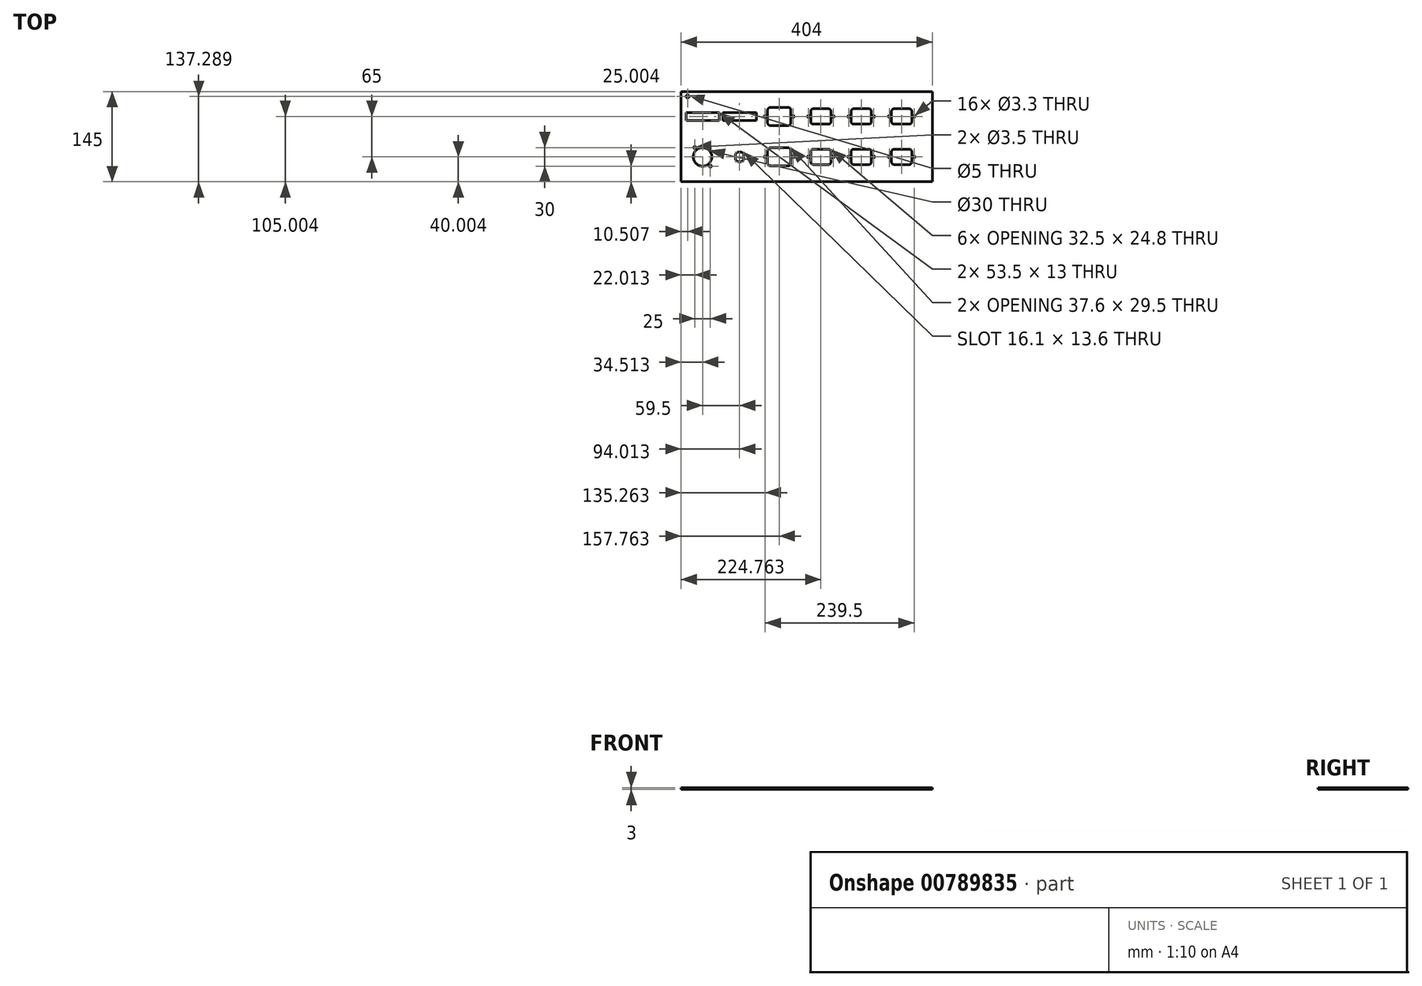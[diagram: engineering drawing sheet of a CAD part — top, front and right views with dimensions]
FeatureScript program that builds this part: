
annotation { "Feature Type Name" : "Feature", "Feature Type Description" : "" }
export const myFeature = defineFeature(function(context is Context, id is Id, definition is map)
    precondition{}
    {
        {
            var Q0;
            Q0=qCreatedBy(makeId("Top.planeOp"),FACE);
            var sketch = newSketch(context, id + "F0", { "sketchPlane" : qUnion([Q0])});
            skLineSegment(sketch, "E0.bottom", {"start": v(-216.19, 64.87) * mm, "end": v(187.81, 64.87) * mm});
            skLineSegment(sketch, "E0.top", {"start": v(-216.19, -80.13) * mm, "end": v(187.81, -80.13) * mm});
            skLineSegment(sketch, "E0.left", {"start": v(-216.19, 64.87) * mm, "end": v(-216.19, -80.13) * mm});
            skLineSegment(sketch, "E0.right", {"start": v(187.81, 64.87) * mm, "end": v(187.81, -80.13) * mm});
            skSolve(sketch);
        }
        {
            var Q0;
            Q0=qCreatedBy(makeId("Top.planeOp"),FACE);
            var sketch = newSketch(context, id + "F1", { "sketchPlane" : qUnion([Q0])});
            skLineSegment(sketch, "E1.bottom", {"start": v(150.82, 12.47) * mm, "end": v(126.32, 12.47) * mm});
            skLineSegment(sketch, "E1.top", {"start": v(150.82, 37.27) * mm, "end": v(126.32, 37.27) * mm});
            skLineSegment(sketch, "E1.left", {"start": v(154.82, 16.47) * mm, "end": v(154.82, 33.27) * mm});
            skLineSegment(sketch, "E1.right", {"start": v(122.32, 16.47) * mm, "end": v(122.32, 33.27) * mm});
            skPoint(sketch, "E1.middle", {"position": v(138.57, 24.87) * mm});
            skPoint(sketch, "E2.visualSharp", {"position": v(122.32, 37.27) * mm});
            skArc(sketch, "E2.filletArc", {"start": v(126.32, 37.27) * mm, "mid": v(123.5, 36.1) * mm, "end": v(122.32, 33.27) * mm});
            skPoint(sketch, "E3.visualSharp", {"position": v(154.82, 37.27) * mm});
            skArc(sketch, "E3.filletArc", {"start": v(154.82, 33.27) * mm, "mid": v(153.65, 36.1) * mm, "end": v(150.82, 37.27) * mm});
            skPoint(sketch, "E4.visualSharp", {"position": v(154.82, 12.47) * mm});
            skArc(sketch, "E4.filletArc", {"start": v(150.82, 12.47) * mm, "mid": v(153.65, 13.65) * mm, "end": v(154.82, 16.47) * mm});
            skPoint(sketch, "E5.visualSharp", {"position": v(122.32, 12.47) * mm});
            skArc(sketch, "E5.filletArc", {"start": v(122.32, 16.47) * mm, "mid": v(123.5, 13.65) * mm, "end": v(126.32, 12.47) * mm});
            skCircle(sketch, "E6", {"center": v(158.57, 24.87) * mm, "radius": 1.5 * mm});
            skCircle(sketch, "E7", {"center": v(118.57, 24.87) * mm, "radius": 1.5 * mm});
            skLineSegment(sketch, "E8.bottom", {"start": v(-44.63, 10.12) * mm, "end": v(-72.23, 10.12) * mm});
            skLineSegment(sketch, "E8.top", {"start": v(-44.63, 39.62) * mm, "end": v(-72.23, 39.62) * mm});
            skLineSegment(sketch, "E8.left", {"start": v(-39.63, 15.12) * mm, "end": v(-39.63, 34.62) * mm});
            skLineSegment(sketch, "E8.right", {"start": v(-77.23, 15.12) * mm, "end": v(-77.23, 34.62) * mm});
            skPoint(sketch, "E8.middle", {"position": v(-58.43, 24.87) * mm});
            skPoint(sketch, "E9.visualSharp", {"position": v(-77.23, 39.62) * mm});
            skArc(sketch, "E9.filletArc", {"start": v(-72.23, 39.62) * mm, "mid": v(-75.76, 38.16) * mm, "end": v(-77.23, 34.62) * mm});
            skPoint(sketch, "E10.visualSharp", {"position": v(-39.63, 39.62) * mm});
            skArc(sketch, "E10.filletArc", {"start": v(-39.63, 34.62) * mm, "mid": v(-41.1, 38.16) * mm, "end": v(-44.63, 39.62) * mm});
            skPoint(sketch, "E11.visualSharp", {"position": v(-39.63, 10.12) * mm});
            skArc(sketch, "E11.filletArc", {"start": v(-44.63, 10.12) * mm, "mid": v(-41.1, 11.59) * mm, "end": v(-39.63, 15.12) * mm});
            skPoint(sketch, "E12.visualSharp", {"position": v(-77.23, 10.12) * mm});
            skArc(sketch, "E12.filletArc", {"start": v(-77.23, 15.12) * mm, "mid": v(-75.76, 11.59) * mm, "end": v(-72.23, 10.12) * mm});
            skCircle(sketch, "E13", {"center": v(-35.93, 24.87) * mm, "radius": 1.5 * mm});
            skCircle(sketch, "E14", {"center": v(-80.93, 24.87) * mm, "radius": 1.5 * mm});
            skLineSegment(sketch, "E15", {"start": v(-85.43, 7.87) * mm, "end": v(-85.43, 41.87) * mm, "construction": true});
            skLineSegment(sketch, "E16", {"start": v(-85.43, 41.87) * mm, "end": v(-31.43, 41.87) * mm, "construction": true});
            skLineSegment(sketch, "E17", {"start": v(-31.43, 41.87) * mm, "end": v(-31.43, 7.87) * mm, "construction": true});
            skLineSegment(sketch, "E18", {"start": v(-31.43, 7.87) * mm, "end": v(-85.43, 7.87) * mm, "construction": true});
            skLineSegment(sketch, "E19", {"start": v(113.57, 38.87) * mm, "end": v(113.57, 10.87) * mm, "construction": true});
            skLineSegment(sketch, "E20", {"start": v(113.57, 10.87) * mm, "end": v(163.57, 10.87) * mm, "construction": true});
            skLineSegment(sketch, "E21", {"start": v(163.57, 10.87) * mm, "end": v(163.57, 38.87) * mm, "construction": true});
            skLineSegment(sketch, "E22", {"start": v(163.57, 38.87) * mm, "end": v(113.57, 38.87) * mm, "construction": true});
            skLineSegment(sketch, "E23.0.1.0", {"start": v(163.57, -26.13) * mm, "end": v(113.57, -26.13) * mm, "construction": true});
            skLineSegment(sketch, "E23.0.1.1", {"start": v(113.57, -26.13) * mm, "end": v(113.57, -54.13) * mm, "construction": true});
            skLineSegment(sketch, "E23.0.1.2", {"start": v(163.57, -54.13) * mm, "end": v(163.57, -26.13) * mm, "construction": true});
            skLineSegment(sketch, "E23.0.1.3", {"start": v(122.32, -48.53) * mm, "end": v(122.32, -31.73) * mm});
            skLineSegment(sketch, "E23.0.1.4", {"start": v(154.82, -48.53) * mm, "end": v(154.82, -31.73) * mm});
            skLineSegment(sketch, "E23.0.1.5", {"start": v(150.82, -27.73) * mm, "end": v(126.32, -27.73) * mm});
            skPoint(sketch, "E23.0.1.6", {"position": v(154.82, -27.73) * mm});
            skLineSegment(sketch, "E23.0.1.7", {"start": v(150.82, -52.53) * mm, "end": v(126.32, -52.53) * mm});
            skLineSegment(sketch, "E23.0.1.8", {"start": v(113.57, -54.13) * mm, "end": v(163.57, -54.13) * mm, "construction": true});
            skPoint(sketch, "E23.0.1.9", {"position": v(138.57, -40.13) * mm});
            skPoint(sketch, "E23.0.1.10", {"position": v(122.32, -52.53) * mm});
            skPoint(sketch, "E23.0.1.11", {"position": v(154.82, -52.53) * mm});
            skPoint(sketch, "E23.0.1.12", {"position": v(122.32, -27.73) * mm});
            skCircle(sketch, "E23.0.1.13", {"center": v(158.57, -40.13) * mm, "radius": 1.5 * mm});
            skCircle(sketch, "E23.0.1.14", {"center": v(118.57, -40.13) * mm, "radius": 1.5 * mm});
            skArc(sketch, "E23.0.1.15", {"start": v(122.32, -48.53) * mm, "mid": v(123.5, -51.35) * mm, "end": v(126.32, -52.53) * mm});
            skArc(sketch, "E23.0.1.16", {"start": v(154.82, -31.73) * mm, "mid": v(153.65, -28.9) * mm, "end": v(150.82, -27.73) * mm});
            skArc(sketch, "E23.0.1.17", {"start": v(150.82, -52.53) * mm, "mid": v(153.65, -51.35) * mm, "end": v(154.82, -48.53) * mm});
            skArc(sketch, "E23.0.1.18", {"start": v(126.32, -27.73) * mm, "mid": v(123.5, -28.9) * mm, "end": v(122.32, -31.73) * mm});
            skLineSegment(sketch, "E23.1.0.0", {"start": v(98.57, 38.87) * mm, "end": v(48.57, 38.87) * mm, "construction": true});
            skLineSegment(sketch, "E23.1.0.1", {"start": v(48.57, 38.87) * mm, "end": v(48.57, 10.87) * mm, "construction": true});
            skLineSegment(sketch, "E23.1.0.2", {"start": v(98.57, 10.87) * mm, "end": v(98.57, 38.87) * mm, "construction": true});
            skLineSegment(sketch, "E23.1.0.3", {"start": v(57.32, 16.47) * mm, "end": v(57.32, 33.27) * mm});
            skLineSegment(sketch, "E23.1.0.4", {"start": v(89.82, 16.47) * mm, "end": v(89.82, 33.27) * mm});
            skLineSegment(sketch, "E23.1.0.5", {"start": v(85.82, 37.27) * mm, "end": v(61.32, 37.27) * mm});
            skPoint(sketch, "E23.1.0.6", {"position": v(89.82, 37.27) * mm});
            skLineSegment(sketch, "E23.1.0.7", {"start": v(85.82, 12.47) * mm, "end": v(61.32, 12.47) * mm});
            skLineSegment(sketch, "E23.1.0.8", {"start": v(48.57, 10.87) * mm, "end": v(98.57, 10.87) * mm, "construction": true});
            skPoint(sketch, "E23.1.0.9", {"position": v(73.57, 24.87) * mm});
            skPoint(sketch, "E23.1.0.10", {"position": v(57.32, 12.47) * mm});
            skPoint(sketch, "E23.1.0.11", {"position": v(89.82, 12.47) * mm});
            skPoint(sketch, "E23.1.0.12", {"position": v(57.32, 37.27) * mm});
            skCircle(sketch, "E23.1.0.13", {"center": v(93.57, 24.87) * mm, "radius": 1.5 * mm});
            skCircle(sketch, "E23.1.0.14", {"center": v(53.57, 24.87) * mm, "radius": 1.5 * mm});
            skArc(sketch, "E23.1.0.15", {"start": v(57.32, 16.47) * mm, "mid": v(58.5, 13.65) * mm, "end": v(61.32, 12.47) * mm});
            skArc(sketch, "E23.1.0.16", {"start": v(89.82, 33.27) * mm, "mid": v(88.65, 36.1) * mm, "end": v(85.82, 37.27) * mm});
            skArc(sketch, "E23.1.0.17", {"start": v(85.82, 12.47) * mm, "mid": v(88.65, 13.65) * mm, "end": v(89.82, 16.47) * mm});
            skArc(sketch, "E23.1.0.18", {"start": v(61.32, 37.27) * mm, "mid": v(58.5, 36.1) * mm, "end": v(57.32, 33.27) * mm});
            skLineSegment(sketch, "E23.1.1.0", {"start": v(98.57, -26.13) * mm, "end": v(48.57, -26.13) * mm, "construction": true});
            skLineSegment(sketch, "E23.1.1.1", {"start": v(48.57, -26.13) * mm, "end": v(48.57, -54.13) * mm, "construction": true});
            skLineSegment(sketch, "E23.1.1.2", {"start": v(98.57, -54.13) * mm, "end": v(98.57, -26.13) * mm, "construction": true});
            skLineSegment(sketch, "E23.1.1.3", {"start": v(57.32, -48.53) * mm, "end": v(57.32, -31.73) * mm});
            skLineSegment(sketch, "E23.1.1.4", {"start": v(89.82, -48.53) * mm, "end": v(89.82, -31.73) * mm});
            skLineSegment(sketch, "E23.1.1.5", {"start": v(85.82, -27.73) * mm, "end": v(61.32, -27.73) * mm});
            skPoint(sketch, "E23.1.1.6", {"position": v(89.82, -27.73) * mm});
            skLineSegment(sketch, "E23.1.1.7", {"start": v(85.82, -52.53) * mm, "end": v(61.32, -52.53) * mm});
            skLineSegment(sketch, "E23.1.1.8", {"start": v(48.57, -54.13) * mm, "end": v(98.57, -54.13) * mm, "construction": true});
            skPoint(sketch, "E23.1.1.9", {"position": v(73.57, -40.13) * mm});
            skPoint(sketch, "E23.1.1.10", {"position": v(57.32, -52.53) * mm});
            skPoint(sketch, "E23.1.1.11", {"position": v(89.82, -52.53) * mm});
            skPoint(sketch, "E23.1.1.12", {"position": v(57.32, -27.73) * mm});
            skCircle(sketch, "E23.1.1.13", {"center": v(93.57, -40.13) * mm, "radius": 1.5 * mm});
            skCircle(sketch, "E23.1.1.14", {"center": v(53.57, -40.13) * mm, "radius": 1.5 * mm});
            skArc(sketch, "E23.1.1.15", {"start": v(57.32, -48.53) * mm, "mid": v(58.5, -51.35) * mm, "end": v(61.32, -52.53) * mm});
            skArc(sketch, "E23.1.1.16", {"start": v(89.82, -31.73) * mm, "mid": v(88.65, -28.9) * mm, "end": v(85.82, -27.73) * mm});
            skArc(sketch, "E23.1.1.17", {"start": v(85.82, -52.53) * mm, "mid": v(88.65, -51.35) * mm, "end": v(89.82, -48.53) * mm});
            skArc(sketch, "E23.1.1.18", {"start": v(61.32, -27.73) * mm, "mid": v(58.5, -28.9) * mm, "end": v(57.32, -31.73) * mm});
            skLineSegment(sketch, "E23.2.0.0", {"start": v(33.57, 38.87) * mm, "end": v(-16.43, 38.87) * mm, "construction": true});
            skLineSegment(sketch, "E23.2.0.1", {"start": v(-16.43, 38.87) * mm, "end": v(-16.43, 10.87) * mm, "construction": true});
            skLineSegment(sketch, "E23.2.0.2", {"start": v(33.57, 10.87) * mm, "end": v(33.57, 38.87) * mm, "construction": true});
            skLineSegment(sketch, "E23.2.0.3", {"start": v(-7.68, 16.47) * mm, "end": v(-7.68, 33.27) * mm});
            skLineSegment(sketch, "E23.2.0.4", {"start": v(24.82, 16.47) * mm, "end": v(24.82, 33.27) * mm});
            skLineSegment(sketch, "E23.2.0.5", {"start": v(20.82, 37.27) * mm, "end": v(-3.68, 37.27) * mm});
            skPoint(sketch, "E23.2.0.6", {"position": v(24.82, 37.27) * mm});
            skLineSegment(sketch, "E23.2.0.7", {"start": v(20.82, 12.47) * mm, "end": v(-3.68, 12.47) * mm});
            skLineSegment(sketch, "E23.2.0.8", {"start": v(-16.43, 10.87) * mm, "end": v(33.57, 10.87) * mm, "construction": true});
            skPoint(sketch, "E23.2.0.9", {"position": v(8.57, 24.87) * mm});
            skPoint(sketch, "E23.2.0.10", {"position": v(-7.68, 12.47) * mm});
            skPoint(sketch, "E23.2.0.11", {"position": v(24.82, 12.47) * mm});
            skPoint(sketch, "E23.2.0.12", {"position": v(-7.68, 37.27) * mm});
            skCircle(sketch, "E23.2.0.13", {"center": v(28.57, 24.87) * mm, "radius": 1.5 * mm});
            skCircle(sketch, "E23.2.0.14", {"center": v(-11.43, 24.87) * mm, "radius": 1.5 * mm});
            skArc(sketch, "E23.2.0.15", {"start": v(-7.68, 16.47) * mm, "mid": v(-6.5, 13.65) * mm, "end": v(-3.68, 12.47) * mm});
            skArc(sketch, "E23.2.0.16", {"start": v(24.82, 33.27) * mm, "mid": v(23.65, 36.1) * mm, "end": v(20.82, 37.27) * mm});
            skArc(sketch, "E23.2.0.17", {"start": v(20.82, 12.47) * mm, "mid": v(23.65, 13.65) * mm, "end": v(24.82, 16.47) * mm});
            skArc(sketch, "E23.2.0.18", {"start": v(-3.68, 37.27) * mm, "mid": v(-6.5, 36.1) * mm, "end": v(-7.68, 33.27) * mm});
            skLineSegment(sketch, "E23.2.1.0", {"start": v(33.57, -26.13) * mm, "end": v(-16.43, -26.13) * mm, "construction": true});
            skLineSegment(sketch, "E23.2.1.1", {"start": v(-16.43, -26.13) * mm, "end": v(-16.43, -54.13) * mm, "construction": true});
            skLineSegment(sketch, "E23.2.1.2", {"start": v(33.57, -54.13) * mm, "end": v(33.57, -26.13) * mm, "construction": true});
            skLineSegment(sketch, "E23.2.1.3", {"start": v(-7.68, -48.53) * mm, "end": v(-7.68, -31.73) * mm});
            skLineSegment(sketch, "E23.2.1.4", {"start": v(24.82, -48.53) * mm, "end": v(24.82, -31.73) * mm});
            skLineSegment(sketch, "E23.2.1.5", {"start": v(20.82, -27.73) * mm, "end": v(-3.68, -27.73) * mm});
            skPoint(sketch, "E23.2.1.6", {"position": v(24.82, -27.73) * mm});
            skLineSegment(sketch, "E23.2.1.7", {"start": v(20.82, -52.53) * mm, "end": v(-3.68, -52.53) * mm});
            skLineSegment(sketch, "E23.2.1.8", {"start": v(-16.43, -54.13) * mm, "end": v(33.57, -54.13) * mm, "construction": true});
            skPoint(sketch, "E23.2.1.9", {"position": v(8.57, -40.13) * mm});
            skPoint(sketch, "E23.2.1.10", {"position": v(-7.68, -52.53) * mm});
            skPoint(sketch, "E23.2.1.11", {"position": v(24.82, -52.53) * mm});
            skPoint(sketch, "E23.2.1.12", {"position": v(-7.68, -27.73) * mm});
            skCircle(sketch, "E23.2.1.13", {"center": v(28.57, -40.13) * mm, "radius": 1.5 * mm});
            skCircle(sketch, "E23.2.1.14", {"center": v(-11.43, -40.13) * mm, "radius": 1.5 * mm});
            skArc(sketch, "E23.2.1.15", {"start": v(-7.68, -48.53) * mm, "mid": v(-6.5, -51.35) * mm, "end": v(-3.68, -52.53) * mm});
            skArc(sketch, "E23.2.1.16", {"start": v(24.82, -31.73) * mm, "mid": v(23.65, -28.9) * mm, "end": v(20.82, -27.73) * mm});
            skArc(sketch, "E23.2.1.17", {"start": v(20.82, -52.53) * mm, "mid": v(23.65, -51.35) * mm, "end": v(24.82, -48.53) * mm});
            skArc(sketch, "E23.2.1.18", {"start": v(-3.68, -27.73) * mm, "mid": v(-6.5, -28.9) * mm, "end": v(-7.68, -31.73) * mm});
            skLineSegment(sketch, "E23.direction1", {"start": v(113.57, 10.87) * mm, "end": v(48.57, 10.87) * mm, "construction": true});
            skLineSegment(sketch, "E23.direction2", {"start": v(113.57, 10.87) * mm, "end": v(113.57, -54.13) * mm, "construction": true});
            skPoint(sketch, "E24.0.1.0", {"position": v(-77.23, -54.88) * mm});
            skPoint(sketch, "E24.0.1.1", {"position": v(-39.63, -54.88) * mm});
            skLineSegment(sketch, "E24.0.1.2", {"start": v(-85.43, -23.13) * mm, "end": v(-31.43, -23.13) * mm, "construction": true});
            skLineSegment(sketch, "E24.0.1.3", {"start": v(-31.43, -23.13) * mm, "end": v(-31.43, -57.13) * mm, "construction": true});
            skPoint(sketch, "E24.0.1.4", {"position": v(-58.43, -40.13) * mm});
            skLineSegment(sketch, "E24.0.1.5", {"start": v(-31.43, -57.13) * mm, "end": v(-85.43, -57.13) * mm, "construction": true});
            skLineSegment(sketch, "E24.0.1.6", {"start": v(-77.23, -49.88) * mm, "end": v(-77.23, -30.38) * mm});
            skLineSegment(sketch, "E24.0.1.7", {"start": v(-85.43, -57.13) * mm, "end": v(-85.43, -23.13) * mm, "construction": true});
            skPoint(sketch, "E24.0.1.8", {"position": v(-77.23, -25.38) * mm});
            skLineSegment(sketch, "E24.0.1.9", {"start": v(-39.63, -49.88) * mm, "end": v(-39.63, -30.38) * mm});
            skLineSegment(sketch, "E24.0.1.10", {"start": v(-44.63, -54.88) * mm, "end": v(-72.23, -54.88) * mm});
            skLineSegment(sketch, "E24.0.1.11", {"start": v(-44.63, -25.38) * mm, "end": v(-72.23, -25.38) * mm});
            skPoint(sketch, "E24.0.1.12", {"position": v(-39.63, -25.38) * mm});
            skCircle(sketch, "E24.0.1.13", {"center": v(-35.93, -40.13) * mm, "radius": 1.5 * mm});
            skArc(sketch, "E24.0.1.14", {"start": v(-72.23, -25.38) * mm, "mid": v(-75.76, -26.84) * mm, "end": v(-77.23, -30.38) * mm});
            skArc(sketch, "E24.0.1.15", {"start": v(-77.23, -49.88) * mm, "mid": v(-75.76, -53.41) * mm, "end": v(-72.23, -54.88) * mm});
            skCircle(sketch, "E24.0.1.16", {"center": v(-80.93, -40.13) * mm, "radius": 1.5 * mm});
            skArc(sketch, "E24.0.1.17", {"start": v(-44.63, -54.88) * mm, "mid": v(-41.1, -53.41) * mm, "end": v(-39.63, -49.88) * mm});
            skArc(sketch, "E24.0.1.18", {"start": v(-39.63, -30.38) * mm, "mid": v(-41.1, -26.84) * mm, "end": v(-44.63, -25.38) * mm});
            skLineSegment(sketch, "E24.direction1", {"start": v(-85.43, 7.87) * mm, "end": v(-79.08, 7.87) * mm, "construction": true});
            skLineSegment(sketch, "E24.direction2", {"start": v(-85.43, 7.87) * mm, "end": v(-85.43, -57.13) * mm, "construction": true});
            skCircle(sketch, "E25", {"center": v(-181.68, -40.13) * mm, "radius": 15 * mm});
            skCircle(sketch, "E26", {"center": v(-169.18, -55.13) * mm, "radius": 1.75 * mm});
            skCircle(sketch, "E27", {"center": v(-194.18, -25.13) * mm, "radius": 1.75 * mm});
            skLineSegment(sketch, "E28.bottom", {"start": v(-154.93, 18.37) * mm, "end": v(-208.43, 18.37) * mm});
            skLineSegment(sketch, "E28.top", {"start": v(-154.93, 31.37) * mm, "end": v(-208.43, 31.37) * mm});
            skLineSegment(sketch, "E28.left", {"start": v(-154.93, 18.37) * mm, "end": v(-154.93, 31.37) * mm});
            skLineSegment(sketch, "E28.right", {"start": v(-208.43, 18.37) * mm, "end": v(-208.43, 31.37) * mm});
            skPoint(sketch, "E28.middle", {"position": v(-181.68, 24.87) * mm});
            skCircle(sketch, "E29", {"center": v(-205.68, 57.16) * mm, "radius": 2.5 * mm});
            skArc(sketch, "E30", {"start": v(-128.98, -44.43) * mm, "mid": v(-122.18, -48.18) * mm, "end": v(-115.38, -44.43) * mm});
            skLineSegment(sketch, "E31", {"start": v(-128.98, -35.82) * mm, "end": v(-128.98, -44.43) * mm});
            skLineSegment(sketch, "E32", {"start": v(-115.38, -35.82) * mm, "end": v(-115.38, -44.43) * mm});
            skArc(sketch, "E33.trimOffspring", {"start": v(-115.38, -35.82) * mm, "mid": v(-122.18, -32.08) * mm, "end": v(-128.98, -35.82) * mm});
            skLineSegment(sketch, "E34.bottom", {"start": v(-95.43, 18.37) * mm, "end": v(-148.93, 18.37) * mm});
            skLineSegment(sketch, "E34.top", {"start": v(-95.43, 31.37) * mm, "end": v(-148.93, 31.37) * mm});
            skLineSegment(sketch, "E34.left", {"start": v(-95.43, 18.37) * mm, "end": v(-95.43, 31.37) * mm});
            skLineSegment(sketch, "E34.right", {"start": v(-148.93, 18.37) * mm, "end": v(-148.93, 31.37) * mm});
            skPoint(sketch, "E34.middle", {"position": v(-122.18, 24.87) * mm});
            skPoint(sketch, "E35", {"position": v(-122.18, 18.37) * mm});
            skSolve(sketch);
        }
        {
            var Q0;
            Q0=makeQuery(id+"F0.imprint","IMPRINT",FACE,{"disambiguationData":[TD([[makeQuery(id+"F0.imprint","IMPRINT",EDGE,{"derivedFrom":sQuery(id+"F0.wireOp",EDGE,"E0.bottom")}),-1.0]])]});
            extrude(context, id + "F2", {"entities" : qUnion([Q0]), "oppositeDirection" : true, "depth" : 3 * mm, "offsetDistance" : 25 * mm});
        }
        {
            var Q0;
            Q0=sQuery(id+"F1.wireOp",VERTEX,"E7.center");
            var Q1;
            Q1=sQuery(id+"F1.wireOp",VERTEX,"E6.center");
            var Q2;
            Q2=sQuery(id+"F1.wireOp",VERTEX,"E23.1.0.13.center");
            var Q3;
            Q3=sQuery(id+"F1.wireOp",VERTEX,"E23.1.0.14.center");
            var Q4;
            Q4=sQuery(id+"F1.wireOp",VERTEX,"E23.1.1.14.center");
            var Q5;
            Q5=sQuery(id+"F1.wireOp",VERTEX,"E23.1.1.13.center");
            var Q6;
            Q6=sQuery(id+"F1.wireOp",VERTEX,"E23.0.1.14.center");
            var Q7;
            Q7=sQuery(id+"F1.wireOp",VERTEX,"E23.0.1.13.center");
            var Q8;
            Q8=sQuery(id+"F1.wireOp",VERTEX,"E23.2.1.13.center");
            var Q9;
            Q9=sQuery(id+"F1.wireOp",VERTEX,"E23.2.1.14.center");
            var Q10;
            Q10=sQuery(id+"F1.wireOp",VERTEX,"E23.2.0.14.center");
            var Q11;
            Q11=sQuery(id+"F1.wireOp",VERTEX,"E23.2.0.13.center");
            var Q12;
            Q12=sQuery(id+"F1.wireOp",VERTEX,"E13.center");
            var Q13;
            Q13=sQuery(id+"F1.wireOp",VERTEX,"E14.center");
            var Q14;
            Q14=sQuery(id+"F1.wireOp",VERTEX,"E24.0.1.16.center");
            var Q15;
            Q15=sQuery(id+"F1.wireOp",VERTEX,"E24.0.1.13.center");
            var Q16;
            Q16=makeQuery(id+"F2.opExtrude","SWEPT_BODY",BODY,{"disambiguationData":[OSD([sQuery(id+"F0.wireOp",EDGE,"E0.bottom"),sQuery(id+"F0.wireOp",EDGE,"E0.top"),sQuery(id+"F0.wireOp",EDGE,"E0.left"),sQuery(id+"F0.wireOp",EDGE,"E0.right")])]});
            hole(context, id + "F3", {"style" : HoleStyle.SIMPLE, "endStyle" : HoleEndStyle.BLIND, "standardTappedOrClearance" : lookupTablePath({ "standard" : "ISO", "engagement" : "75%", "pitch" : "0.7 mm", "size" : "M4", "type" : "Tapped" }), "standardBlindInLast" : lookupTablePath({ "standard" : "ISO", "engagement" : "75%", "pitch" : "0.7 mm", "size" : "M4", "type" : "Tapped" }), "holeDiameter" : 3.3 * mm, "majorDiameter" : 4 * mm, "showTappedDepth" : true, "holeDepth" : 8.6 * mm, "isTappedThrough" : true, "tappedDepth" : 6.5 * mm, "tapClearance" : 3, "locations" : qUnion([Q0, Q1, Q2, Q3, Q4, Q5, Q6, Q7, Q8, Q9, Q10, Q11, Q12, Q13, Q14, Q15]), "scope" : qUnion([Q16])});
        }
        {
            var Q0;
            Q0 = qSketchRegion(id + "F1", true);
            extrude(context, id + "F4", {"entities" : qUnion([Q0]), "operationType" : NewBodyOperationType.REMOVE, "oppositeDirection" : true, "depth" : 25 * mm, "offsetDistance" : 25 * mm});
        }
    });
